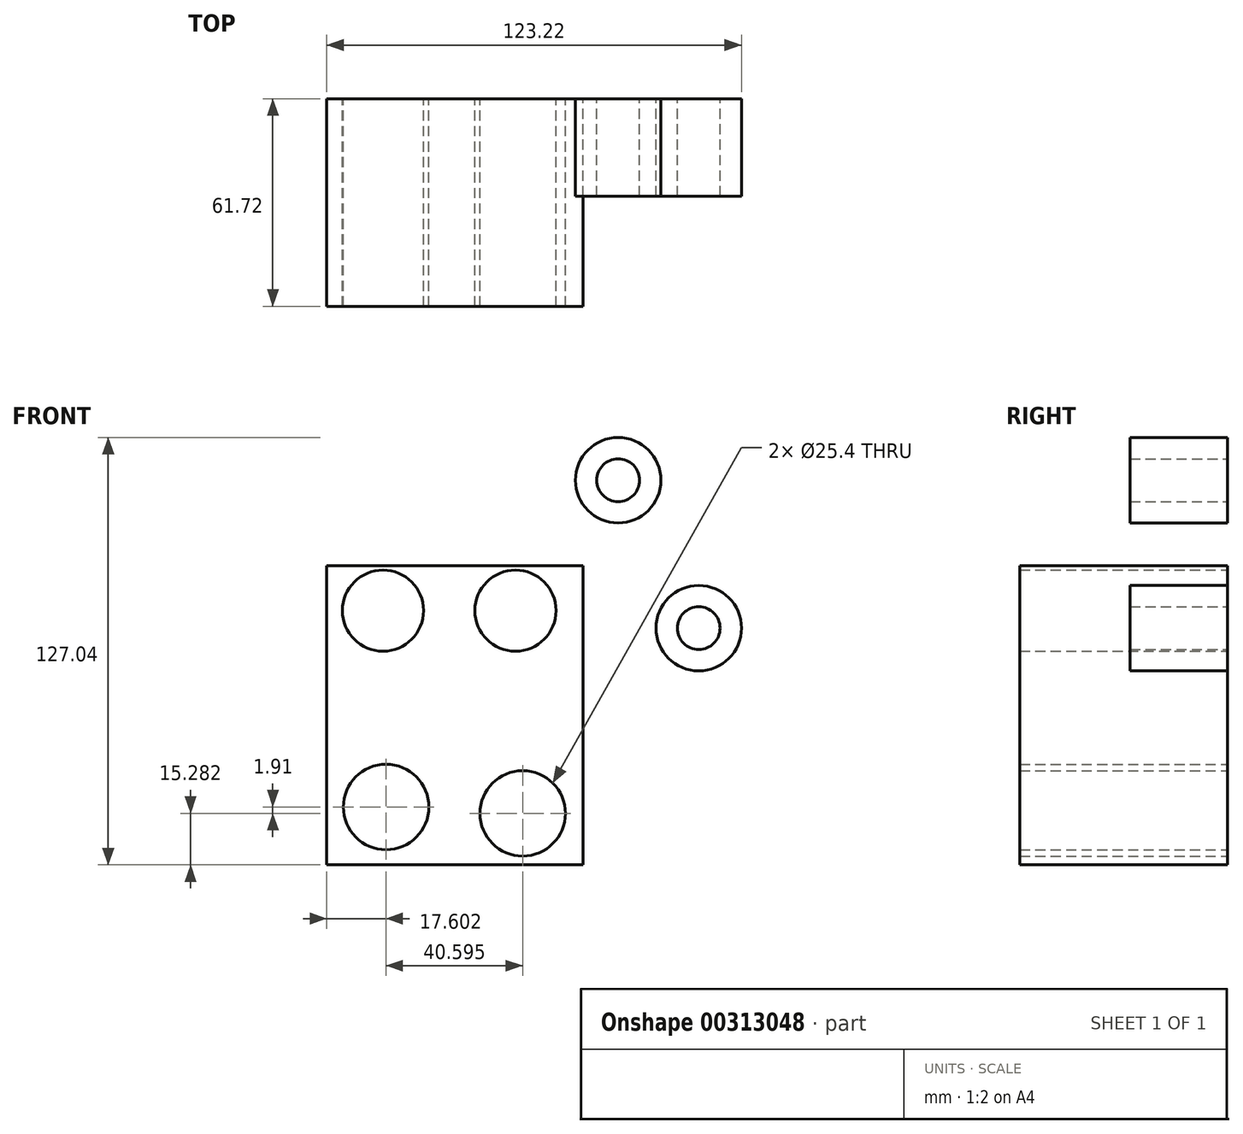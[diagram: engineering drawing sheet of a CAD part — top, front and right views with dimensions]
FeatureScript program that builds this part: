
annotation { "Feature Type Name" : "Feature", "Feature Type Description" : "" }
export const myFeature = defineFeature(function(context is Context, id is Id, definition is map)
    precondition{}
    {
        {
            var Q0;
            Q0=qCreatedBy(makeId("Front.planeOp"),FACE);
            var sketch = newSketch(context, id + "F0", { "sketchPlane" : qUnion([Q0])});
            skLineSegment(sketch, "E0.bottom", {"start": v(-125.66, 20.61) * mm, "end": v(-49.46, 20.61) * mm});
            skLineSegment(sketch, "E0.top", {"start": v(-125.66, -68.29) * mm, "end": v(-49.46, -68.29) * mm});
            skLineSegment(sketch, "E0.left", {"start": v(-125.66, 20.61) * mm, "end": v(-125.66, -68.29) * mm});
            skLineSegment(sketch, "E0.right", {"start": v(-49.46, 20.61) * mm, "end": v(-49.46, -68.29) * mm});
            skCircle(sketch, "E1", {"center": v(-108.97, 7.28) * mm, "radius": 12.07 * mm});
            skCircle(sketch, "E2", {"center": v(-69.6, 7.28) * mm, "radius": 12.07 * mm});
            skCircle(sketch, "E3", {"center": v(-108.06, -51.1) * mm, "radius": 12.7 * mm});
            skCircle(sketch, "E4", {"center": v(-67.46, -53) * mm, "radius": 12.7 * mm});
            skSolve(sketch);
        }
        {
            var Q0;
            Q0 = qSketchRegion(id + "F0", true);
            extrude(context, id + "F1", {"entities" : qUnion([Q0]), "depth" : 61.72 * mm});
        }
        {
            var Q0;
            Q0=qCreatedBy(makeId("Front.planeOp"),FACE);
            var sketch = newSketch(context, id + "F2", { "sketchPlane" : qUnion([Q0])});
            skCircle(sketch, "E5", {"center": v(-39.07, 46.05) * mm, "radius": 12.7 * mm});
            skCircle(sketch, "E6", {"center": v(-15.14, 2.08) * mm, "radius": 12.7 * mm});
            skCircle(sketch, "E7", {"center": v(-39.07, 46.05) * mm, "radius": 6.35 * mm});
            skCircle(sketch, "E8", {"center": v(-15.14, 2.08) * mm, "radius": 6.35 * mm});
            skSolve(sketch);
        }
        {
            var Q0;
            Q0 = qSketchRegion(id + "F2", true);
            extrude(context, id + "F3", {"entities" : qUnion([Q0]), "depth" : 28.96 * mm});
        }
    });
